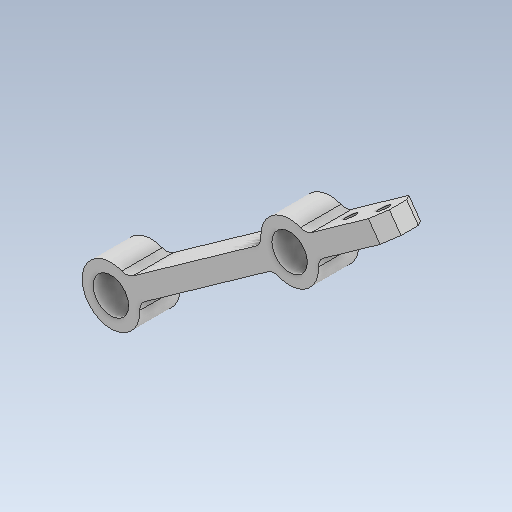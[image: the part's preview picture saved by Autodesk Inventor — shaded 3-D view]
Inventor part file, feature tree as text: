
AUTODESK INVENTOR PART (.ipt)
format: ipt  version: 2023 (Build 270158000, 158)  size: 131,072 bytes
history: native  units: mm
features: other x3, sketch x2
ambient origin geometry x8: Origin, YZ Plane, XZ Plane, XY Plane, X Axis, Y Axis, Z Axis, Center Point
bodies: Solid1 (feature_tree)
feature tree (5):
  other  "leg_link_1.ipt"
  other  "Solid1::leg_link_1.ipt"
  other  "TaggingFeature1"
  sketch  "Sketch1"  dims[d0=10.0mm]
  sketch  "Sketch2"
